# Revit family: Edge_TB42_F_Side_Hung_Standard
name_source: partatom
category: Windows
revit_build: Autodesk Revit 2014 (Build: 20130308_1515(x64)
units: mm (PartAtom-declared; Revit-internal decimal feet)

## types (12) — shared parameters
Aluminium Thickness = 1 mm  [stored 0.00328084 ft]
Area Pane Left Top = 0.52 m²
Area Pane Right Top = 0.52 m²
Bead SG Gap = 13 mm
Casement Dimension = 42 mm  [stored 0.137795 ft]
Custom Sash Left Height = 1154 mm  [stored 3.78609 ft]
Custom Sash Left Width = 554 mm  [stored 1.81759 ft]
Custom Sash Right Height = 1154 mm  [stored 3.78609 ft]
Custom Sash Right Width = 554 mm  [stored 1.81759 ft]
DG Extrusion Start = 11 mm  [stored 0.0360892 ft]
DG Gasket Finish = Double Glazing Gasket Material
DG Thickness Calc = 4 mm  [stored 0.0131234 ft]
Default Sill Height = 800 mm  [stored 2.62467 ft]
Depth Bead = 28 mm  [stored 0.0918635 ft]
Depth Mullion = 1 mm  [stored 0.00328084 ft]
Description = Thermal break casement windows (42mm), Type F side hung
Frame Center Offset = 21 mm  [stored 0.0688976 ft]
Has Stiffener Cap = Yes
Height Sash Left = 1124 mm  [stored 3.68766 ft]
Height Sash Left Opening = 1154 mm  [stored 3.78609 ft]
Height Sash Right = 1124 mm  [stored 3.68766 ft]
Height Sash Right Opening = 1154 mm  [stored 3.78609 ft]
Length Transom Left = 540 mm  [stored 1.77165 ft]
Length Transom Right = 540 mm  [stored 1.77165 ft]
Limit Fixed Pane Height Max = 1800 mm  [stored 5.90551 ft]
Limit Fixed Pane Height Min = 200 mm  [stored 0.656168 ft]
Limit Fixed Pane Width Max = 1500 mm  [stored 4.92126 ft]
Limit Fixed Pane Width Min = 200 mm  [stored 0.656168 ft]
Limit Sash Height Max = 1500 mm  [stored 4.92126 ft]
Limit Sash Height Min = 300 mm  [stored 0.984252 ft]
Limit Sash Width Max = 700 mm  [stored 2.29659 ft]
Limit Sash Width Min = 300 mm  [stored 0.984252 ft]
Limit Window Height Max = 1860 mm
Limit Window Height Min = 1430 mm  [stored 4.6916 ft]
Limit Window Width Max = 2700 mm
Limit Window Width Min = 1400 mm
Manufacturer = Crealco
Max System DG One Piece Thickness = 6 mm  [stored 0.019685 ft]
Max System DG Unit Thickness = 25 mm  [stored 0.082021 ft]
Model = Edge
Mullion Depth Windload Based = 1 mm  [stored 0.00328084 ft]
Offset Bead Center Reversed = 21 mm  [stored 0.0688976 ft]
Offset Fixed Panel Center Left = 600 mm  [stored 1.9685 ft]
Offset Mullion Left = 570 mm  [stored 1.87008 ft]
Offset Mullion Right = 570 mm  [stored 1.87008 ft]
Offset Sash Side = 23 mm  [stored 0.0754593 ft]
Offset Sash Top = 23 mm  [stored 0.0754593 ft]
Offset Transom Left Top = 1170 mm
Offset Transom Right Top = 1170 mm
Offset Window Exterior = 21 mm  [stored 0.0688976 ft]
SG Gasket Thickness = 6 mm  [stored 0.019685 ft]
Sash Center Offset = 18 mm
Sash Overlap = 7 mm  [stored 0.0229659 ft]
Sash Spacing Inner = 8 mm  [stored 0.0262467 ft]
Side Hung Left = Yes
Side Hung Right = No
URL = http://www.crealco.co.za
Wall Closure = By host
Width Bead = 15 mm  [stored 0.0492126 ft]
Width Fixed Panel Left = 540 mm  [stored 1.77165 ft]
Width Fixed Panel Right = 540 mm  [stored 1.77165 ft]
Width Profile = 30 mm  [stored 0.0984252 ft]
Width Sash Left = 524 mm  [stored 1.71916 ft]
Width Sash Left Opening = 554 mm  [stored 1.81759 ft]
Width Sash Right = 524 mm  [stored 1.71916 ft]
Width Sash Right Opening = 554 mm  [stored 1.81759 ft]
zero-valued in all types: Window Exterior Offset

## per-type parameters (varying)
- EDGE-1815SS-1000Pa: Area Pane Left Bottom=0.13 m²; Area Pane Middle=0.82 m²; Area Pane Right Bottom=0.13 m²; Clearvue Insulated LowE SHGC Value=0.587; Clearvue Insulated LowE U Value=2.26; Clearvue Insulated SHGC Value=0.646; Clearvue Insulated U Value=2.82; Clearvue SHGC Value=0.723; Clearvue U Value=5.24; Custom Windload=1000 mm  [stored 3.28084 ft]; Custom Window Height=1490 mm  [stored 4.88845 ft]; Custom Window Width=1790 mm  [stored 5.8727 ft]; Energy Advantage SHGC Value=0.646; Energy Advantage U Value=3.69; Height=1490 mm  [stored 4.88845 ft]; Height Fixed Panel Center=1430 mm  [stored 4.6916 ft]; Height Fixed Panel Left=260 mm; Height Fixed Panel Right=260 mm; Intruderprufe Insulated LowE SHGC Value=0.536; Intruderprufe Insulated LowE U Value=2.22; Intruderprufe Insulated SHGC Value=0.594; Intruderprufe Insulated U Value=2.78; Intruderprufe LowE SHGC Value=0.601; Intruderprufe LowE U Value=3.67; Intruderprufe SHGC Value=0.676; Intruderprufe U Value=5.14; Length Mullion=1490 mm  [stored 4.88845 ft]; Max Pane Area=0.82 m²; Width=1790 mm  [stored 5.8727 ft]; Width Fixed Panel Center=590 mm; Windload Design=1000 mm  [stored 3.28084 ft]
- EDGE-2415SS-1000Pa: Area Pane Left Bottom=0.13 m²; Area Pane Middle=1.68 m²; Area Pane Right Bottom=0.13 m²; Clearvue Insulated LowE SHGC Value=0.635; Clearvue Insulated LowE U Value=2.33; Clearvue Insulated SHGC Value=0.699; Clearvue Insulated U Value=2.98; Clearvue SHGC Value=0; Clearvue U Value=7.9; Custom Windload=1000 mm  [stored 3.28084 ft]; Custom Window Height=1490 mm  [stored 4.88845 ft]; Custom Window Width=2390 mm; Energy Advantage SHGC Value=0; Energy Advantage U Value=7.9; Height=1490 mm  [stored 4.88845 ft]; Height Fixed Panel Center=1430 mm  [stored 4.6916 ft]; Height Fixed Panel Left=260 mm; Height Fixed Panel Right=260 mm; Intruderprufe Insulated LowE SHGC Value=0.58; Intruderprufe Insulated LowE U Value=2.29; Intruderprufe Insulated SHGC Value=0.643; Intruderprufe Insulated U Value=2.93; Intruderprufe LowE SHGC Value=0.651; Intruderprufe LowE U Value=3.89; Intruderprufe SHGC Value=0.734; Intruderprufe U Value=5.58; Length Mullion=1490 mm  [stored 4.88845 ft]; Max Pane Area=1.68 m²; Width=2390 mm; Width Fixed Panel Center=1190 mm; Windload Design=1000 mm  [stored 3.28084 ft]
- EDGE-1818SS-1000Pa: Area Pane Left Bottom=0.29 m²; Area Pane Middle=1 m²; Area Pane Right Bottom=0.29 m²; Clearvue Insulated LowE SHGC Value=0.63; Clearvue Insulated LowE U Value=2.36; Clearvue Insulated SHGC Value=0.693; Clearvue Insulated U Value=2.97; Clearvue SHGC Value=0.776; Clearvue U Value=5.59; Custom Windload=1000 mm  [stored 3.28084 ft]; Custom Window Height=1790 mm  [stored 5.8727 ft]; Custom Window Width=1790 mm  [stored 5.8727 ft]; Energy Advantage SHGC Value=0.693; Energy Advantage U Value=3.91; Height=1790 mm  [stored 5.8727 ft]; Height Fixed Panel Center=1730 mm  [stored 5.67585 ft]; Height Fixed Panel Left=560 mm; Height Fixed Panel Right=560 mm; Intruderprufe Insulated LowE SHGC Value=0.575; Intruderprufe Insulated LowE U Value=2.32; Intruderprufe Insulated SHGC Value=0.638; Intruderprufe Insulated U Value=2.93; Intruderprufe LowE SHGC Value=0.645; Intruderprufe LowE U Value=3.87; Intruderprufe SHGC Value=0.726; Intruderprufe U Value=5.48; Length Mullion=1790 mm  [stored 5.8727 ft]; Max Pane Area=1 m²; Width=1790 mm  [stored 5.8727 ft]; Width Fixed Panel Center=590 mm; Windload Design=1000 mm  [stored 3.28084 ft]
- EDGE-2418SS-1000Pa: Area Pane Left Bottom=0.29 m²; Area Pane Middle=2.03 m²; Area Pane Right Bottom=0.29 m²; Clearvue Insulated LowE SHGC Value=0.699; Clearvue Insulated LowE U Value=2.5; Clearvue Insulated SHGC Value=0.769; Clearvue Insulated U Value=3.22; Clearvue SHGC Value=0; Clearvue U Value=7.9; Custom Windload=1000 mm  [stored 3.28084 ft]; Custom Window Height=1790 mm  [stored 5.8727 ft]; Custom Window Width=2390 mm; Energy Advantage SHGC Value=0; Energy Advantage U Value=7.9; Height=1790 mm  [stored 5.8727 ft]; Height Fixed Panel Center=1730 mm  [stored 5.67585 ft]; Height Fixed Panel Left=560 mm; Height Fixed Panel Right=560 mm; Intruderprufe Insulated LowE SHGC Value=0.639; Intruderprufe Insulated LowE U Value=2.46; Intruderprufe Insulated SHGC Value=0.708; Intruderprufe Insulated U Value=3.17; Intruderprufe LowE SHGC Value=0.717; Intruderprufe LowE U Value=4.21; Intruderprufe SHGC Value=0.809; Intruderprufe U Value=6.1; Length Mullion=1790 mm  [stored 5.8727 ft]; Max Pane Area=2.03 m²; Width=2390 mm; Width Fixed Panel Center=1190 mm; Windload Design=1000 mm  [stored 3.28084 ft]
- EDGE-1815SS-1500Pa: Area Pane Left Bottom=0.13 m²; Area Pane Middle=0.82 m²; Area Pane Right Bottom=0.13 m²; Clearvue Insulated LowE SHGC Value=0.587; Clearvue Insulated LowE U Value=2.26; Clearvue Insulated SHGC Value=0.646; Clearvue Insulated U Value=2.82; Clearvue SHGC Value=0.723; Clearvue U Value=5.24; Custom Windload=1500 mm  [stored 4.92126 ft]; Custom Window Height=1490 mm  [stored 4.88845 ft]; Custom Window Width=1790 mm  [stored 5.8727 ft]; Energy Advantage SHGC Value=0.646; Energy Advantage U Value=3.69; Height=1490 mm  [stored 4.88845 ft]; Height Fixed Panel Center=1430 mm  [stored 4.6916 ft]; Height Fixed Panel Left=260 mm; Height Fixed Panel Right=260 mm; Intruderprufe Insulated LowE SHGC Value=0.536; Intruderprufe Insulated LowE U Value=2.22; Intruderprufe Insulated SHGC Value=0.594; Intruderprufe Insulated U Value=2.78; Intruderprufe LowE SHGC Value=0.601; Intruderprufe LowE U Value=3.67; Intruderprufe SHGC Value=0.676; Intruderprufe U Value=5.14; Length Mullion=1490 mm  [stored 4.88845 ft]; Max Pane Area=0.82 m²; Width=1790 mm  [stored 5.8727 ft]; Width Fixed Panel Center=590 mm; Windload Design=1500 mm  [stored 4.92126 ft]
- EDGE-1815SS-2000Pa: Area Pane Left Bottom=0.13 m²; Area Pane Middle=0.82 m²; Area Pane Right Bottom=0.13 m²; Clearvue Insulated LowE SHGC Value=0.587; Clearvue Insulated LowE U Value=2.26; Clearvue Insulated SHGC Value=0.646; Clearvue Insulated U Value=2.82; Clearvue SHGC Value=0.723; Clearvue U Value=5.24; Custom Windload=2000 mm; Custom Window Height=1490 mm  [stored 4.88845 ft]; Custom Window Width=1790 mm  [stored 5.8727 ft]; Energy Advantage SHGC Value=0.646; Energy Advantage U Value=3.69; Height=1490 mm  [stored 4.88845 ft]; Height Fixed Panel Center=1430 mm  [stored 4.6916 ft]; Height Fixed Panel Left=260 mm; Height Fixed Panel Right=260 mm; Intruderprufe Insulated LowE SHGC Value=0.536; Intruderprufe Insulated LowE U Value=2.22; Intruderprufe Insulated SHGC Value=0.594; Intruderprufe Insulated U Value=2.78; Intruderprufe LowE SHGC Value=0.601; Intruderprufe LowE U Value=3.67; Intruderprufe SHGC Value=0.676; Intruderprufe U Value=5.14; Length Mullion=1490 mm  [stored 4.88845 ft]; Max Pane Area=0.82 m²; Width=1790 mm  [stored 5.8727 ft]; Width Fixed Panel Center=590 mm; Windload Design=2000 mm
- EDGE-2415SS-1500Pa: Area Pane Left Bottom=0.13 m²; Area Pane Middle=1.68 m²; Area Pane Right Bottom=0.13 m²; Clearvue Insulated LowE SHGC Value=0.635; Clearvue Insulated LowE U Value=2.33; Clearvue Insulated SHGC Value=0.699; Clearvue Insulated U Value=2.98; Clearvue SHGC Value=0; Clearvue U Value=7.9; Custom Windload=1500 mm  [stored 4.92126 ft]; Custom Window Height=1490 mm  [stored 4.88845 ft]; Custom Window Width=2390 mm; Energy Advantage SHGC Value=0; Energy Advantage U Value=7.9; Height=1490 mm  [stored 4.88845 ft]; Height Fixed Panel Center=1430 mm  [stored 4.6916 ft]; Height Fixed Panel Left=260 mm; Height Fixed Panel Right=260 mm; Intruderprufe Insulated LowE SHGC Value=0.58; Intruderprufe Insulated LowE U Value=2.29; Intruderprufe Insulated SHGC Value=0.643; Intruderprufe Insulated U Value=2.93; Intruderprufe LowE SHGC Value=0.651; Intruderprufe LowE U Value=3.89; Intruderprufe SHGC Value=0.734; Intruderprufe U Value=5.58; Length Mullion=1490 mm  [stored 4.88845 ft]; Max Pane Area=1.68 m²; Width=2390 mm; Width Fixed Panel Center=1190 mm; Windload Design=1500 mm  [stored 4.92126 ft]
- EDGE-2415SS-2000Pa: Area Pane Left Bottom=0.13 m²; Area Pane Middle=1.68 m²; Area Pane Right Bottom=0.13 m²; Clearvue Insulated LowE SHGC Value=0.635; Clearvue Insulated LowE U Value=2.33; Clearvue Insulated SHGC Value=0.699; Clearvue Insulated U Value=2.98; Clearvue SHGC Value=0; Clearvue U Value=7.9; Custom Windload=2000 mm; Custom Window Height=1490 mm  [stored 4.88845 ft]; Custom Window Width=2390 mm; Energy Advantage SHGC Value=0; Energy Advantage U Value=7.9; Height=1490 mm  [stored 4.88845 ft]; Height Fixed Panel Center=1430 mm  [stored 4.6916 ft]; Height Fixed Panel Left=260 mm; Height Fixed Panel Right=260 mm; Intruderprufe Insulated LowE SHGC Value=0.58; Intruderprufe Insulated LowE U Value=2.29; Intruderprufe Insulated SHGC Value=0.643; Intruderprufe Insulated U Value=2.93; Intruderprufe LowE SHGC Value=0.651; Intruderprufe LowE U Value=3.89; Intruderprufe SHGC Value=0.734; Intruderprufe U Value=5.58; Length Mullion=1490 mm  [stored 4.88845 ft]; Max Pane Area=1.68 m²; Width=2390 mm; Width Fixed Panel Center=1190 mm; Windload Design=2000 mm
- EDGE-1818SS-1500Pa: Area Pane Left Bottom=0.29 m²; Area Pane Middle=1 m²; Area Pane Right Bottom=0.29 m²; Clearvue Insulated LowE SHGC Value=0.63; Clearvue Insulated LowE U Value=2.36; Clearvue Insulated SHGC Value=0.693; Clearvue Insulated U Value=2.97; Clearvue SHGC Value=0.776; Clearvue U Value=5.59; Custom Windload=1500 mm  [stored 4.92126 ft]; Custom Window Height=1790 mm  [stored 5.8727 ft]; Custom Window Width=1790 mm  [stored 5.8727 ft]; Energy Advantage SHGC Value=0.693; Energy Advantage U Value=3.91; Height=1790 mm  [stored 5.8727 ft]; Height Fixed Panel Center=1730 mm  [stored 5.67585 ft]; Height Fixed Panel Left=560 mm; Height Fixed Panel Right=560 mm; Intruderprufe Insulated LowE SHGC Value=0.575; Intruderprufe Insulated LowE U Value=2.32; Intruderprufe Insulated SHGC Value=0.638; Intruderprufe Insulated U Value=2.93; Intruderprufe LowE SHGC Value=0.645; Intruderprufe LowE U Value=3.87; Intruderprufe SHGC Value=0.726; Intruderprufe U Value=5.48; Length Mullion=1790 mm  [stored 5.8727 ft]; Max Pane Area=1 m²; Width=1790 mm  [stored 5.8727 ft]; Width Fixed Panel Center=590 mm; Windload Design=1500 mm  [stored 4.92126 ft]
- EDGE-1818SS-2000Pa: Area Pane Left Bottom=0.29 m²; Area Pane Middle=1 m²; Area Pane Right Bottom=0.29 m²; Clearvue Insulated LowE SHGC Value=0.63; Clearvue Insulated LowE U Value=2.36; Clearvue Insulated SHGC Value=0.693; Clearvue Insulated U Value=2.97; Clearvue SHGC Value=0.776; Clearvue U Value=5.59; Custom Windload=2000 mm; Custom Window Height=1790 mm  [stored 5.8727 ft]; Custom Window Width=1790 mm  [stored 5.8727 ft]; Energy Advantage SHGC Value=0.693; Energy Advantage U Value=3.91; Height=1790 mm  [stored 5.8727 ft]; Height Fixed Panel Center=1730 mm  [stored 5.67585 ft]; Height Fixed Panel Left=560 mm; Height Fixed Panel Right=560 mm; Intruderprufe Insulated LowE SHGC Value=0.575; Intruderprufe Insulated LowE U Value=2.32; Intruderprufe Insulated SHGC Value=0.638; Intruderprufe Insulated U Value=2.93; Intruderprufe LowE SHGC Value=0.645; Intruderprufe LowE U Value=3.87; Intruderprufe SHGC Value=0.726; Intruderprufe U Value=5.48; Length Mullion=1790 mm  [stored 5.8727 ft]; Max Pane Area=1 m²; Width=1790 mm  [stored 5.8727 ft]; Width Fixed Panel Center=590 mm; Windload Design=2000 mm
- EDGE-2418SS-1500Pa: Area Pane Left Bottom=0.29 m²; Area Pane Middle=2.03 m²; Area Pane Right Bottom=0.29 m²; Clearvue Insulated LowE SHGC Value=0.699; Clearvue Insulated LowE U Value=2.5; Clearvue Insulated SHGC Value=0.769; Clearvue Insulated U Value=3.22; Clearvue SHGC Value=0; Clearvue U Value=7.9; Custom Windload=1500 mm  [stored 4.92126 ft]; Custom Window Height=1790 mm  [stored 5.8727 ft]; Custom Window Width=2390 mm; Energy Advantage SHGC Value=0; Energy Advantage U Value=7.9; Height=1790 mm  [stored 5.8727 ft]; Height Fixed Panel Center=1730 mm  [stored 5.67585 ft]; Height Fixed Panel Left=560 mm; Height Fixed Panel Right=560 mm; Intruderprufe Insulated LowE SHGC Value=0.639; Intruderprufe Insulated LowE U Value=2.46; Intruderprufe Insulated SHGC Value=0.708; Intruderprufe Insulated U Value=3.17; Intruderprufe LowE SHGC Value=0.717; Intruderprufe LowE U Value=4.21; Intruderprufe SHGC Value=0.809; Intruderprufe U Value=6.1; Length Mullion=1790 mm  [stored 5.8727 ft]; Max Pane Area=2.03 m²; Width=2390 mm; Width Fixed Panel Center=1190 mm; Windload Design=1500 mm  [stored 4.92126 ft]
- EDGE-2418SS-2000Pa: Area Pane Left Bottom=0.29 m²; Area Pane Middle=2.03 m²; Area Pane Right Bottom=0.29 m²; Clearvue Insulated LowE SHGC Value=0.699; Clearvue Insulated LowE U Value=2.5; Clearvue Insulated SHGC Value=0.769; Clearvue Insulated U Value=3.22; Clearvue SHGC Value=0; Clearvue U Value=7.9; Custom Windload=2000 mm; Custom Window Height=1790 mm  [stored 5.8727 ft]; Custom Window Width=2390 mm; Energy Advantage SHGC Value=0; Energy Advantage U Value=7.9; Height=1790 mm  [stored 5.8727 ft]; Height Fixed Panel Center=1730 mm  [stored 5.67585 ft]; Height Fixed Panel Left=560 mm; Height Fixed Panel Right=560 mm; Intruderprufe Insulated LowE SHGC Value=0.639; Intruderprufe Insulated LowE U Value=2.46; Intruderprufe Insulated SHGC Value=0.708; Intruderprufe Insulated U Value=3.17; Intruderprufe LowE SHGC Value=0.717; Intruderprufe LowE U Value=4.21; Intruderprufe SHGC Value=0.809; Intruderprufe U Value=6.1; Length Mullion=1790 mm  [stored 5.8727 ft]; Max Pane Area=2.03 m²; Width=2390 mm; Width Fixed Panel Center=1190 mm; Windload Design=2000 mm

note: [stored X ft] marks values corroborated as IEEE doubles in the binary element streams (Revit-internal decimal feet)

## geometry (parser evidence)
native form markers: Extrusion x1, Sweep x30
no freeform markers — native parametric forms only
